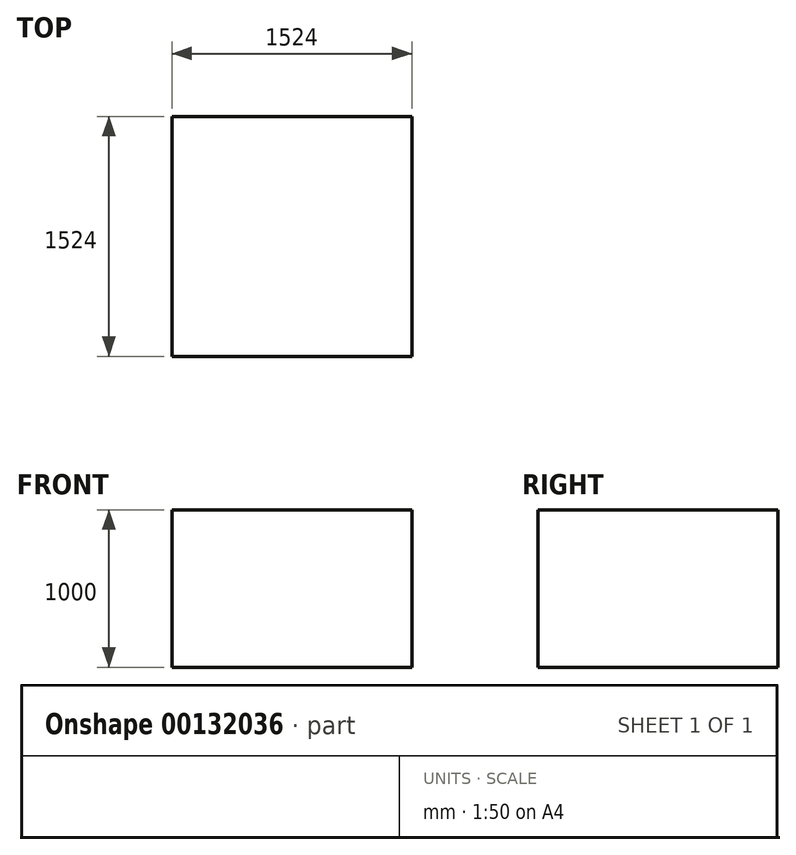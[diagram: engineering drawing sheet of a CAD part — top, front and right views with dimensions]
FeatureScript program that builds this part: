
annotation { "Feature Type Name" : "Feature", "Feature Type Description" : "" }
export const myFeature = defineFeature(function(context is Context, id is Id, definition is map)
    precondition{}
    {
        {
            var Q0;
            Q0=qCreatedBy(makeId("Top.planeOp"),FACE);
            var sketch = newSketch(context, id + "F0", { "sketchPlane" : qUnion([Q0])});
            skLineSegment(sketch, "E0.bottom", {"start": v(762, 762) * mm, "end": v(-762, 762) * mm});
            skLineSegment(sketch, "E0.top", {"start": v(762, -762) * mm, "end": v(-762, -762) * mm});
            skLineSegment(sketch, "E0.left", {"start": v(762, 762) * mm, "end": v(762, -762) * mm});
            skLineSegment(sketch, "E0.right", {"start": v(-762, 762) * mm, "end": v(-762, -762) * mm});
            skPoint(sketch, "E0.middle", {"position": v(0, 0) * mm});
            skSolve(sketch);
        }
        {
            var Q0;
            Q0 = qSketchRegion(id + "F0", true);
            extrude(context, id + "F1", {"entities" : qUnion([Q0]), "depth" : 1000 * mm});
        }
    });
